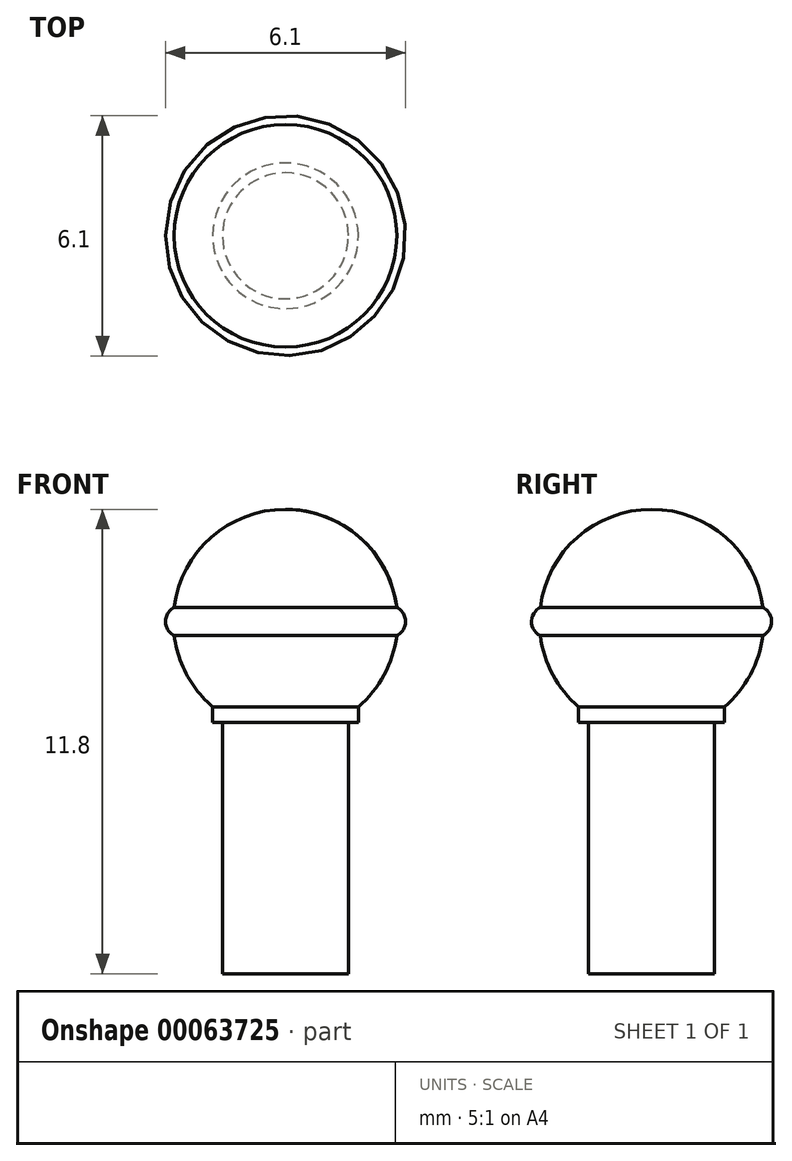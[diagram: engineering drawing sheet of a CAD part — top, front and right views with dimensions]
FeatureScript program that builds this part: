
annotation { "Feature Type Name" : "Feature", "Feature Type Description" : "" }
export const myFeature = defineFeature(function(context is Context, id is Id, definition is map)
    precondition{}
    {
        {
            var Q0;
            Q0=qCreatedBy(makeId("Front.planeOp"),FACE);
            var sketch = newSketch(context, id + "F0", { "sketchPlane" : qUnion([Q0])});
            skLineSegment(sketch, "E0", {"start": v(0, 0) * mm, "end": v(0, 16.86) * mm, "construction": true});
            skArc(sketch, "E1", {"start": v(1.85, 6.78) * mm, "mid": v(2.5, 7.6) * mm, "end": v(2.83, 8.6) * mm});
            skLineSegment(sketch, "E2.bottom", {"start": v(0, 0) * mm, "end": v(1.6, 0) * mm});
            skLineSegment(sketch, "E2.left", {"start": v(0, 0) * mm, "end": v(0, 11.8) * mm});
            skLineSegment(sketch, "E2.right", {"start": v(1.6, 0) * mm, "end": v(1.6, 6.38) * mm});
            skArc(sketch, "E3", {"start": v(2.83, 8.6) * mm, "mid": v(3.05, 8.95) * mm, "end": v(2.83, 9.3) * mm});
            skLineSegment(sketch, "E4.bottom", {"start": v(1.6, 6.38) * mm, "end": v(1.85, 6.38) * mm});
            skLineSegment(sketch, "E4.right", {"start": v(1.85, 6.38) * mm, "end": v(1.85, 6.78) * mm});
            skArc(sketch, "E5.trimOffspring", {"start": v(2.83, 9.3) * mm, "mid": v(1.88, 11.09) * mm, "end": v(0, 11.8) * mm});
            skSolve(sketch);
        }
        {
            var Q0;
            Q0=makeQuery(id+"F0.imprint","IMPRINT",FACE,{"disambiguationData":[TD([[makeQuery(id+"F0.imprint","IMPRINT",EDGE,{"derivedFrom":sQuery(id+"F0.wireOp",EDGE,"E1")}),1.0]])]});
            var Q1;
            Q1=sQuery(id+"F0.wireOp",EDGE,"E0");
            revolve(context, id + "F1", {"entities" : qUnion([Q0]), "axis" : qUnion([Q1]), "revolveType" : RevolveType.FULL});
        }
    });
